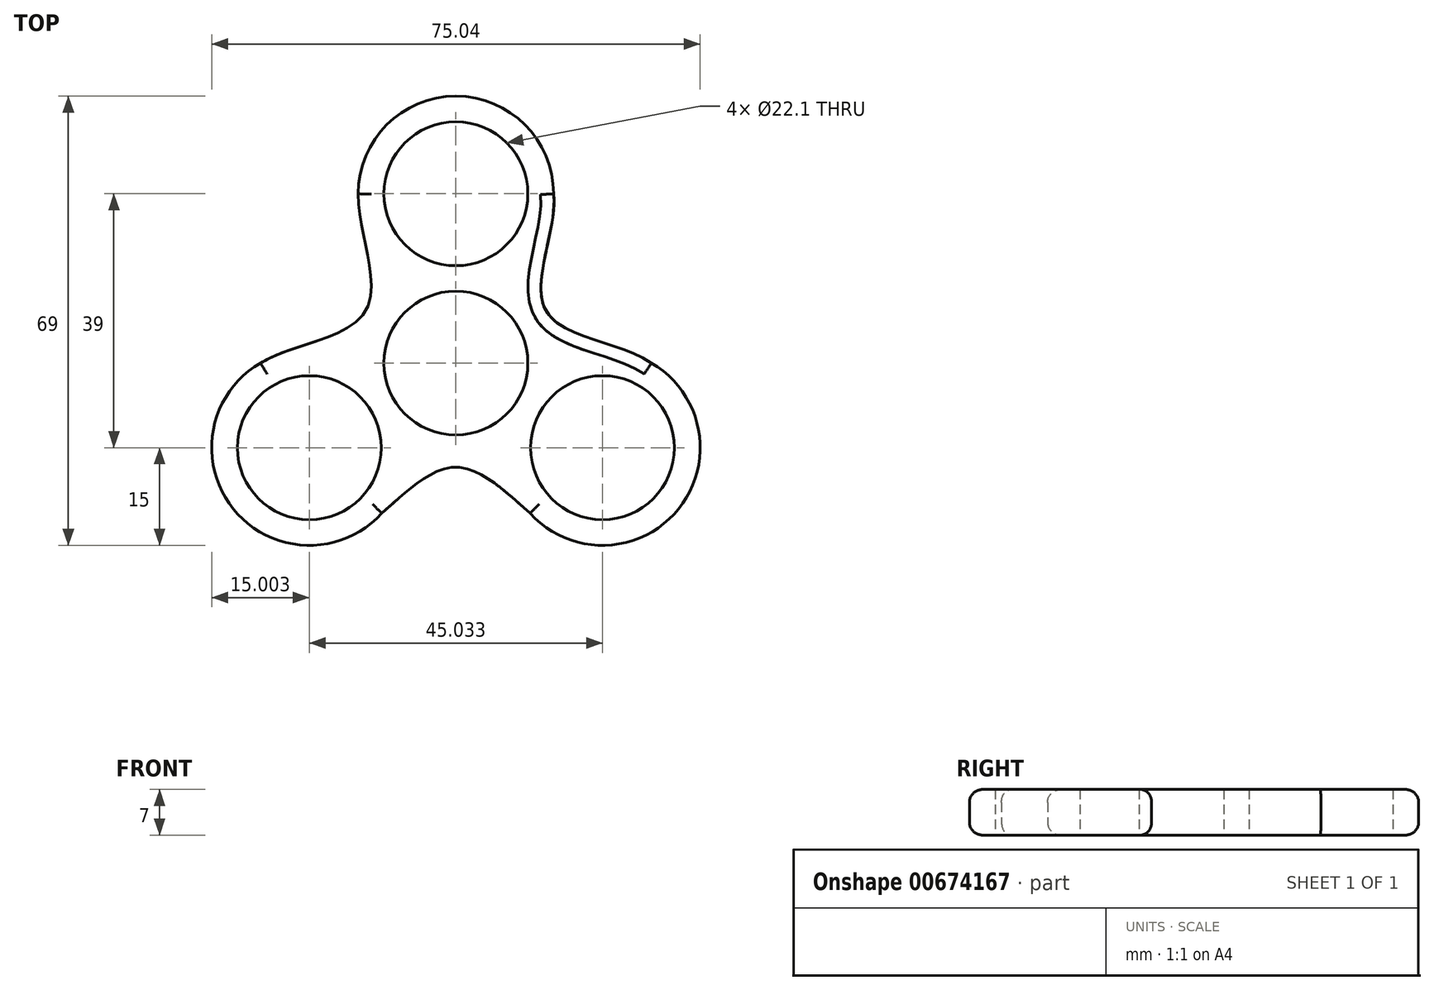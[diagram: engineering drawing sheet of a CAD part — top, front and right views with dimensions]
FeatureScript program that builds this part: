
annotation { "Feature Type Name" : "Feature", "Feature Type Description" : "" }
export const myFeature = defineFeature(function(context is Context, id is Id, definition is map)
    precondition{}
    {
        {
            var Q0;
            Q0=qCreatedBy(makeId("Top.planeOp"),FACE);
            var sketch = newSketch(context, id + "F0", { "sketchPlane" : qUnion([Q0])});
            skCircle(sketch, "E0", {"center": v(0, 0) * mm, "radius": 11.05 * mm});
            skCircle(sketch, "E1", {"center": v(0, 0) * mm, "radius": 15 * mm});
            skCircle(sketch, "E2", {"center": v(0, 26) * mm, "radius": 11.05 * mm});
            skCircle(sketch, "E3", {"center": v(0, 26) * mm, "radius": 15 * mm});
            skLineSegment(sketch, "E4", {"start": v(0, 26) * mm, "end": v(0, 0) * mm, "construction": true});
            skCircle(sketch, "E5", {"center": v(-22.52, -13) * mm, "radius": 11.05 * mm});
            skCircle(sketch, "E6", {"center": v(-22.52, -13) * mm, "radius": 15 * mm});
            skLineSegment(sketch, "E7", {"start": v(-22.52, -13) * mm, "end": v(0, 0) * mm, "construction": true});
            skCircle(sketch, "E8", {"center": v(22.52, -13) * mm, "radius": 11.05 * mm});
            skCircle(sketch, "E9", {"center": v(22.52, -13) * mm, "radius": 15 * mm});
            skLineSegment(sketch, "E10", {"start": v(0, 0) * mm, "end": v(22.52, -13) * mm, "construction": true});
            skLineSegment(sketch, "E11", {"start": v(0, 0) * mm, "end": v(0, -15) * mm, "construction": true});
            skLineSegment(sketch, "E12", {"start": v(0, 0) * mm, "end": v(27.71, 16) * mm, "construction": true});
            skLineSegment(sketch, "E13", {"start": v(-22.52, -13) * mm, "end": v(-41.49, -23.95) * mm, "construction": true});
            skLineSegment(sketch, "E14", {"start": v(-22.52, -13) * mm, "end": v(-39.47, 16.36) * mm, "construction": true});
            skLineSegment(sketch, "E15", {"start": v(0, 26) * mm, "end": v(32.09, 26) * mm, "construction": true});
            skLineSegment(sketch, "E16", {"start": v(32.09, 26) * mm, "end": v(-26.83, 26) * mm, "construction": true});
            skLineSegment(sketch, "E17", {"start": v(22.52, -13) * mm, "end": v(35.25, 9.06) * mm, "construction": true});
            skLineSegment(sketch, "E18", {"start": v(35.25, 9.06) * mm, "end": v(9.41, -35.7) * mm, "construction": true});
            skLineSegment(sketch, "E19", {"start": v(-22.52, -13) * mm, "end": v(-8.32, -37.6) * mm, "construction": true});
            skFitSpline(sketch, "E20", {"points": [v(-30.02, 0) * mm, v(-13.86, 8) * mm, v(-15, 26) * mm], "startDerivative": vector(28.88, 18) * mm, "endDerivative": vector(1.16, 34.01) * mm});
            skLineSegment(sketch, "E21", {"start": v(0, 0) * mm, "end": v(-13, 7.5) * mm, "construction": true});
            skFitSpline(sketch, "E22", {"points": [v(-15.02, -26) * mm, v(0, -16) * mm, v(15.02, -26) * mm], "startDerivative": vector(30.03, 21.01) * mm, "endDerivative": vector(30.03, -21.01) * mm});
            skPoint(sketch, "E23.2.internal.snap0", {"position": v(16.04, 26) * mm});
            skFitSpline(sketch, "E23", {"points": [v(30.02, 0) * mm, v(13.86, 8) * mm, v(15, 26) * mm], "startDerivative": vector(-26.24, 19.53) * mm, "endDerivative": vector(-3.8, 32.49) * mm});
            skSolve(sketch);
        }
        {
            var Q0;
            Q0 = qSketchRegion(id + "F0", true);
            var Q1;
            {var subQ4=sQuery(id+"F0.wireOp",EDGE,"E6");var subQ7=sQuery(id+"F0.wireOp",EDGE,"E0");var subQ8=makeQuery(id+"F0.imprint","INTERSECT",VERTEX,{"disambiguationData":[OD(0.0)],"derivedFrom":[subQ7,subQ4]});Q1=makeQuery(id+"F0.imprint","IMPRINT",FACE,{"disambiguationData":[TD([[makeQuery(id+"F0.imprint","IMPRINT",EDGE,{"disambiguationData":[TD([[subQ8,-1.0]])],"derivedFrom":subQ7}),-1.0]])]});}
            var Q2;
            {var subQ0=sQuery(id+"F0.wireOp",EDGE,"E6");var subQ1=sQuery(id+"F0.wireOp",EDGE,"E0");var subQ2=makeQuery(id+"F0.imprint","INTERSECT",VERTEX,{"disambiguationData":[OD(1.0)],"derivedFrom":[subQ1,subQ0]});Q2=makeQuery(id+"F0.imprint","IMPRINT",FACE,{"disambiguationData":[TD([[makeQuery(id+"F0.imprint","IMPRINT",EDGE,{"disambiguationData":[TD([[subQ2,-1.0]])],"derivedFrom":subQ1}),-1.0]])]});}
            var Q3;
            {var subQ4=sQuery(id+"F0.wireOp",EDGE,"E9");var subQ6=sQuery(id+"F0.wireOp",EDGE,"E0");var subQ9=makeQuery(id+"F0.imprint","INTERSECT",VERTEX,{"disambiguationData":[OD(0.0)],"derivedFrom":[subQ6,subQ4]});Q3=makeQuery(id+"F0.imprint","IMPRINT",FACE,{"disambiguationData":[TD([[makeQuery(id+"F0.imprint","IMPRINT",EDGE,{"disambiguationData":[TD([[subQ9,-1.0]])],"derivedFrom":subQ6}),-1.0]])]});}
            var Q4;
            {var subQ0=sQuery(id+"F0.wireOp",EDGE,"E3");var subQ1=sQuery(id+"F0.wireOp",EDGE,"E0");var subQ2=makeQuery(id+"F0.imprint","INTERSECT",VERTEX,{"disambiguationData":[OD(1.0)],"derivedFrom":[subQ1,subQ0]});Q4=makeQuery(id+"F0.imprint","IMPRINT",FACE,{"disambiguationData":[TD([[makeQuery(id+"F0.imprint","IMPRINT",EDGE,{"disambiguationData":[TD([[subQ2,1.0]])],"derivedFrom":subQ1}),-1.0]])]});}
            var Q5;
            {var subQ4=sQuery(id+"F0.wireOp",EDGE,"E3");var subQ7=sQuery(id+"F0.wireOp",EDGE,"E0");var subQ8=makeQuery(id+"F0.imprint","INTERSECT",VERTEX,{"disambiguationData":[OD(0.0)],"derivedFrom":[subQ7,subQ4]});Q5=makeQuery(id+"F0.imprint","IMPRINT",FACE,{"disambiguationData":[TD([[makeQuery(id+"F0.imprint","IMPRINT",EDGE,{"disambiguationData":[TD([[subQ8,1.0]])],"derivedFrom":subQ7}),-1.0]])]});}
            var Q6;
            {var subQ0=sQuery(id+"F0.wireOp",EDGE,"E3");var subQ1=sQuery(id+"F0.wireOp",EDGE,"E0");var subQ2=makeQuery(id+"F0.imprint","INTERSECT",VERTEX,{"disambiguationData":[OD(0.0)],"derivedFrom":[subQ1,subQ0]});Q6=makeQuery(id+"F0.imprint","IMPRINT",FACE,{"disambiguationData":[TD([[makeQuery(id+"F0.imprint","IMPRINT",EDGE,{"disambiguationData":[TD([[subQ2,-1.0]])],"derivedFrom":subQ1}),-1.0]])]});}
            extrude(context, id + "F1", {"entities" : qUnion([Q0, Q1, Q2, Q3, Q4, Q5, Q6]), "depth" : 7 * mm, "offsetDistance" : 25 * mm});
        }
        {
            var Q0;
            Q0=makeQuery(id+"F1.opExtrude","CAP_EDGE",EDGE,{"disambiguationData":[OSD([sQuery(id+"F0.wireOp",EDGE,"E20")])],"isStart":false});
            var Q1;
            Q1=makeQuery(id+"F1.opExtrude","CAP_EDGE",EDGE,{"disambiguationData":[OSD([sQuery(id+"F0.wireOp",EDGE,"E22")])],"isStart":false});
            var Q2;
            Q2=makeQuery(id+"F1.opExtrude","CAP_EDGE",EDGE,{"disambiguationData":[OSD([sQuery(id+"F0.wireOp",EDGE,"E23")])],"isStart":false});
            var Q3;
            Q3=makeQuery(id+"F1.opExtrude","CAP_EDGE",EDGE,{"disambiguationData":[OSD([sQuery(id+"F0.wireOp",EDGE,"E3")])],"isStart":false});
            var Q4;
            Q4=makeQuery(id+"F1.opExtrude","CAP_EDGE",EDGE,{"disambiguationData":[OSD([sQuery(id+"F0.wireOp",EDGE,"E9")])],"isStart":false});
            var Q5;
            Q5=makeQuery(id+"F1.opExtrude","CAP_EDGE",EDGE,{"disambiguationData":[OSD([sQuery(id+"F0.wireOp",EDGE,"E6")])],"isStart":false});
            fillet(context, id + "F2", {"entities" : qUnion([Q0, Q1, Q2, Q3, Q4, Q5]), "radius" : 2 * mm, "tangentPropagation" : true, "allowEdgeOverflow" : false});
        }
        {
            var Q0;
            Q0=makeQuery(id+"F1.opExtrude","CAP_EDGE",EDGE,{"disambiguationData":[OSD([sQuery(id+"F0.wireOp",EDGE,"E22")])],"isStart":true});
            var Q1;
            Q1=makeQuery(id+"F1.opExtrude","CAP_EDGE",EDGE,{"disambiguationData":[OSD([sQuery(id+"F0.wireOp",EDGE,"E20")])],"isStart":true});
            var Q2;
            Q2=makeQuery(id+"F1.opExtrude","CAP_EDGE",EDGE,{"disambiguationData":[OSD([sQuery(id+"F0.wireOp",EDGE,"E23")])],"isStart":true});
            var Q3;
            Q3=makeQuery(id+"F1.opExtrude","CAP_EDGE",EDGE,{"disambiguationData":[OSD([sQuery(id+"F0.wireOp",EDGE,"E9")])],"isStart":true});
            var Q4;
            Q4=makeQuery(id+"F1.opExtrude","CAP_EDGE",EDGE,{"disambiguationData":[OSD([sQuery(id+"F0.wireOp",EDGE,"E3")])],"isStart":true});
            var Q5;
            Q5=makeQuery(id+"F1.opExtrude","CAP_EDGE",EDGE,{"disambiguationData":[OSD([sQuery(id+"F0.wireOp",EDGE,"E6")])],"isStart":true});
            fillet(context, id + "F3", {"entities" : qUnion([Q0, Q1, Q2, Q3, Q4, Q5]), "radius" : 2 * mm, "tangentPropagation" : true, "allowEdgeOverflow" : false});
        }
    });
